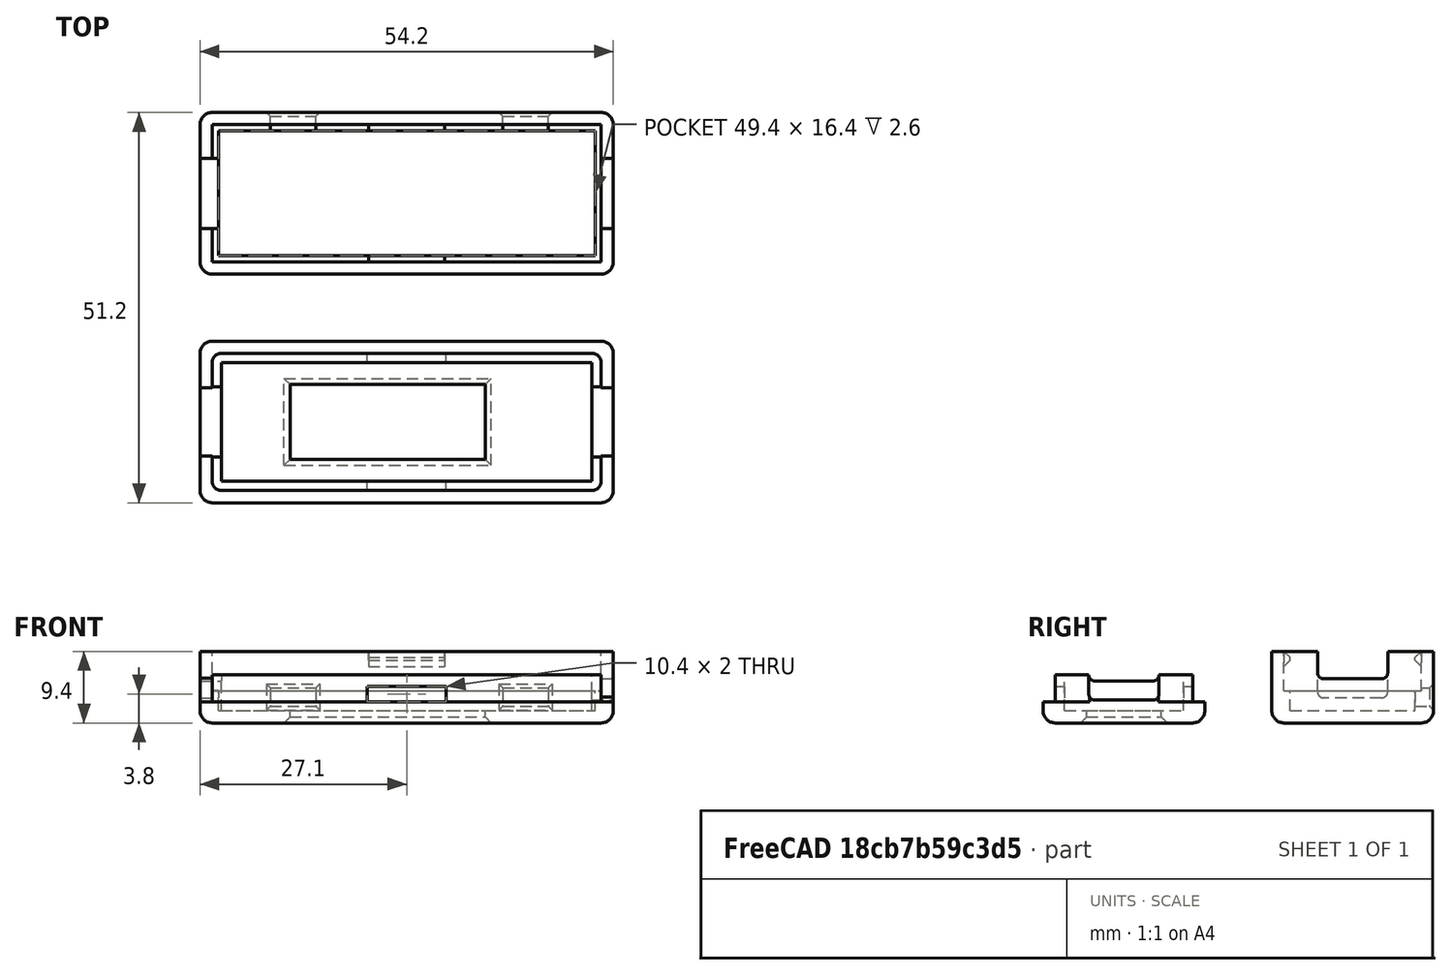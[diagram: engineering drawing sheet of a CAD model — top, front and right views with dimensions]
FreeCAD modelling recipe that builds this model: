
FCSTD DOCUMENT  (FreeCAD 0.16R)
Label: USB-C_Tester_b_v0.4
License: All rights reserved
LicenseURL: http://en.wikipedia.org/wiki/All_rights_reserved
objects: Part::Box×21, Part::Fillet×7, Part::Cut×6, Part::Chamfer×4, Part::MultiFuse×4
note: 42 computed .brp shape members not serialized (recipe doc carries the construction recipe); baked Part::Feature solids carry a one-line shape summary decoded from their .brp

FEATURE [Part::Box] Box  label="unten_außen"
  Height = 9.4
  Length = 54.2
  Placement = pos=(-1.6,-1.6,0) rot=(0,0,1;0rad)
  Width = 21.2
FEATURE [Part::Box] Box001  label="unten_innen"
  Height = 9.4
  Length = 51
  Placement = pos=(0,0,1.6) rot=(0,0,1;0rad)
  Width = 18
FEATURE [Part::Cut] Cut  label="Schale_roh"
  Base = -> Box
  Tool = -> Box001
FEATURE [Part::Fillet] Fillet  label="Schale_unten"
  Base = -> Cut
  Edges = 8 edges r=1.6: [Edge1,Edge3,Edge4,Edge5,Edge6,Edge14,Edge15,Edge16]
FEATURE [Part::Box] Box002  label="Auflage_außen"
  Height = 2.6
  Length = 51
  Placement = pos=(0,0,1.6) rot=(0,0,1;0rad)
  Width = 18
FEATURE [Part::Box] Box003  label="Auflage_innen"
  Height = 2.6
  Length = 49.4
  Placement = pos=(0.8,0.8,1.6) rot=(0,0,1;0rad)
  Width = 16.4
FEATURE [Part::Cut] Cut001  label="Auflage"
  Base = -> Box002
  Tool = -> Box003
FEATURE [Part::Box] Box004  label="Haken1_roh"
  Height = 2
  Length = 10
  Placement = pos=(20.5,-0.2,7.4) rot=(0,0,1;0rad)
  Width = 1
FEATURE [Part::Chamfer] Chamfer  label="Haken1"
  Base = -> Box004
  Edges = 2 edges r=0.8: [Edge11,Edge12]
FEATURE [Part::Box] Box005  label="Haken2_roh"
  Height = 2
  Length = 10
  Placement = pos=(20.5,17.2,7.4) rot=(0,0,1;0rad)
  Width = 1
FEATURE [Part::Chamfer] Chamfer001  label="Haken2"
  Base = -> Box005
  Edges = 2 edges r=0.8: [Edge9,Edge10]
FEATURE [Part::Box] Box006  label="USB_Buchse1_roh"
  Height = 7
  Length = 10
  Placement = pos=(-5,4.4,3.3) rot=(0,0,1;0rad)
  Width = 9.2
FEATURE [Part::Box] Box008  label="Button1"
  Height = 2.4
  Length = 6
  Placement = pos=(7.6,14,2.2) rot=(0,0,1;0rad)
  Width = 10
FEATURE [Part::Box] Box009  label="Button2"
  Height = 2.4
  Length = 6
  Placement = pos=(38.1,14,2.2) rot=(0,0,1;0rad)
  Width = 10
FEATURE [Part::Box] Box010  label="oben_außen"
  Height = 2.8
  Length = 54.2
  Placement = pos=(-1.6,-31.6,0) rot=(0,0,1;0rad)
  Width = 21.2
FEATURE [Part::Box] Box011  label="oben_innen"
  Height = 9.4
  Length = 51
  Placement = pos=(0,-30,1.6) rot=(0,0,1;0rad)
  Width = 18
FEATURE [Part::Cut] Cut002  label="Schale_oben_roh"
  Base = -> Box010
  Tool = -> Box011
FEATURE [Part::Fillet] Fillet001  label="Schale_oben"
  Base = -> Cut002
  Edges = 8 edges r=1.6: [Edge1,Edge3,Edge4,Edge5,Edge6,Edge14,Edge15,Edge16]
FEATURE [Part::Box] Box012  label="Rahmen_außen"
  Height = 4.7
  Length = 51
  Placement = pos=(0,-30,1.6) rot=(0,0,1;0rad)
  Width = 18
FEATURE [Part::Box] Box013  label="Rahmen_innen"
  Height = 4.8
  Length = 48.6
  Placement = pos=(1.2,-28.8,1.6) rot=(0,0,1;0rad)
  Width = 15.6
FEATURE [Part::Cut] Cut003  label="Rahmen"
  Base = -> Box012
  Tool = -> Box013
FEATURE [Part::Box] Box014  label="OLED"
  Height = 1.6
  Length = 25.6
  Placement = pos=(10.2,-25.9,0) rot=(0,0,1;0rad)
  Width = 9.8
FEATURE [Part::Box] Box017  label="Oese1"
  Height = 2
  Length = 10.4
  Placement = pos=(20.3,-33,2.8) rot=(0,0,1;0rad)
  Width = 5
FEATURE [Part::Box] Box018  label="Oese2"
  Height = 2
  Length = 10.4
  Placement = pos=(20.3,-15,2.8) rot=(0,0,1;0rad)
  Width = 5
FEATURE [Part::Box] Box019  label="USB_Buchse2_roh"
  Height = 7
  Length = 10
  Placement = pos=(47,4.4,5.8) rot=(0,0,1;0rad)
  Width = 9.2
FEATURE [Part::Box] Box020  label="USB_Buchse3_roh"
  Height = 4.6
  Length = 10
  Placement = pos=(-5,-25.6,5.5) rot=(0,0,1;0rad)
  Width = 9.2
FEATURE [Part::Box] Box021  label="USB_Buchse4_roh"
  Height = 6
  Length = 10
  Placement = pos=(47,-25.6,3) rot=(0,0,1;0rad)
  Width = 9.2
FEATURE [Part::Fillet] Fillet002  label="USB_Buchse1"
  Base = -> Box006
  Edges = 2 edges r=0.8: [Edge9,Edge11]
FEATURE [Part::Fillet] Fillet003  label="USB_Buchse2"
  Base = -> Box019
  Edges = 2 edges r=0.8: [Edge9,Edge11]
FEATURE [Part::Box] Box022  label="Nut1"
  Height = 5
  Length = 1.6
  Placement = pos=(-1.6,-25.5,2.8) rot=(0,0,1;0rad)
  Width = 9
FEATURE [Part::Box] Box023  label="Nut2"
  Height = 5
  Length = 1.6
  Placement = pos=(51,-25.5,2.8) rot=(0,0,1;0rad)
  Width = 9
FEATURE [Part::Fillet] Fillet004  label="USB-Buchse3"
  Base = -> Box020
  Edges = 2 edges r=0.8: [Edge9,Edge11]
FEATURE [Part::Fillet] Fillet005  label="USB-Buchse4"
  Base = -> Box021
  Edges = 2 edges r=0.8: [Edge9,Edge11]
FEATURE [Part::MultiFuse] Fusion  label="bottom_raw"
  Shapes = -> [Fillet,Cut001,Chamfer,Chamfer001]
FEATURE [Part::MultiFuse] Fusion001  label="bottom_cutouts"
  Shapes = -> [Box008,Box009,Fillet002,Fillet003]
FEATURE [Part::MultiFuse] Fusion002  label="top_raw"
  Shapes = -> [Fillet001,Cut003,Box022,Box023]
FEATURE [Part::MultiFuse] Fusion003  label="top_cutouts"
  Shapes = -> [Box014,Box017,Box018,Fillet004,Fillet005]
FEATURE [Part::Cut] Cut004  label="bottom_raw2"
  Base = -> Fusion
  Tool = -> Fusion001
FEATURE [Part::Cut] Cut005  label="top_raw2"
  Base = -> Fusion002
  Tool = -> Fusion003
FEATURE [Part::Chamfer] Chamfer002  label="case_bottom"
  Base = -> Cut004
  Edges = 8 edges r=0.5: [Edge101,Edge102,Edge103,Edge104,Edge105,Edge106,Edge107,Edge108]
FEATURE [Part::Chamfer] Chamfer003  label="top_raw3"
  Base = -> Cut005
  Edges = 4 edges r=0.8: [Edge122,Edge123,Edge124,Edge125]
FEATURE [Part::Fillet] Fillet006  label="case_top"
  Base = -> Chamfer003
  Edges = 4 edges r=1.2: [Edge129,Edge132,Edge144,Edge146]
